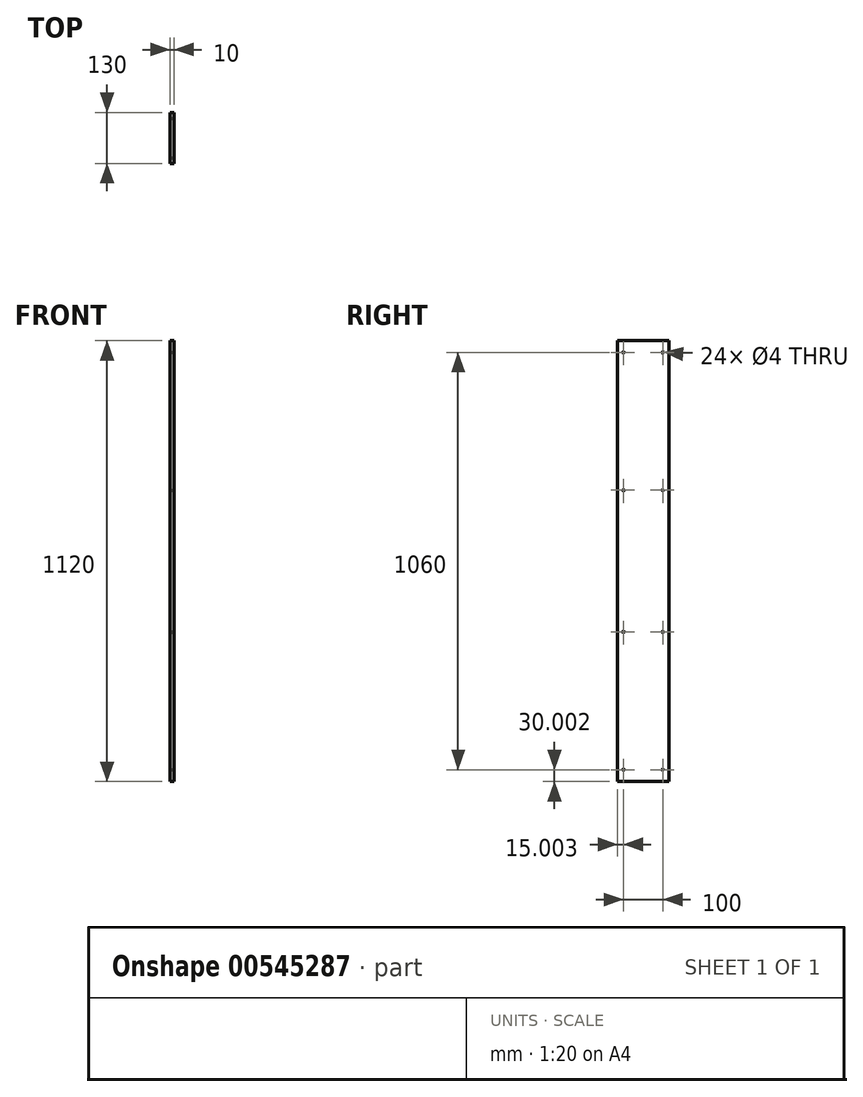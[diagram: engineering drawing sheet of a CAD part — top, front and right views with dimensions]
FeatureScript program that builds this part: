
annotation { "Feature Type Name" : "Feature", "Feature Type Description" : "" }
export const myFeature = defineFeature(function(context is Context, id is Id, definition is map)
    precondition{}
    {
        {
            var Q0;
            Q0=qCreatedBy(makeId("Right.planeOp"),FACE);
            var sketch = newSketch(context, id + "F0", { "sketchPlane" : qUnion([Q0])});
            skLineSegment(sketch, "E0.bottom", {"start": v(-510.9, -532.09) * mm, "end": v(-380.9, -532.09) * mm});
            skLineSegment(sketch, "E0.top", {"start": v(-510.9, 587.91) * mm, "end": v(-380.9, 587.91) * mm});
            skLineSegment(sketch, "E0.left", {"start": v(-510.9, -532.09) * mm, "end": v(-510.9, 587.91) * mm});
            skLineSegment(sketch, "E0.right", {"start": v(-380.9, -532.09) * mm, "end": v(-380.9, 587.91) * mm});
            skSolve(sketch);
        }
        {
            var Q0;
            Q0=makeQuery(id+"F0.imprint","IMPRINT",FACE,{"disambiguationData":[TD([[makeQuery(id+"F0.imprint","IMPRINT",EDGE,{"derivedFrom":sQuery(id+"F0.wireOp",EDGE,"E0.bottom")}),1.0]])]});
            extrude(context, id + "F1", {"entities" : qUnion([Q0]), "depth" : 10 * mm, "offsetDistance" : 25 * mm});
        }
        {
            var Q0;
            Q0=makeQuery(id+"F1.opExtrude","CAP_FACE",FACE,{"disambiguationData":[OSD([sQuery(id+"F0.wireOp",EDGE,"E0.bottom"),sQuery(id+"F0.wireOp",EDGE,"E0.top"),sQuery(id+"F0.wireOp",EDGE,"E0.left"),sQuery(id+"F0.wireOp",EDGE,"E0.right")])],"isStart":false});
            var sketch = newSketch(context, id + "F2", { "sketchPlane" : qUnion([Q0])});
            skLineSegment(sketch, "E1.bottom", {"start": v(-395.9, 557.91) * mm, "end": v(-495.9, 557.91) * mm, "construction": true});
            skLineSegment(sketch, "E1.top", {"start": v(-395.9, -502.09) * mm, "end": v(-495.9, -502.09) * mm, "construction": true});
            skLineSegment(sketch, "E1.left", {"start": v(-395.9, 557.91) * mm, "end": v(-395.9, -502.09) * mm, "construction": true});
            skLineSegment(sketch, "E1.right", {"start": v(-495.9, 557.91) * mm, "end": v(-495.9, -502.09) * mm, "construction": true});
            skPoint(sketch, "E2", {"position": v(-495.9, 557.91) * mm});
            skPoint(sketch, "E3", {"position": v(-395.9, 557.91) * mm});
            skPoint(sketch, "E4", {"position": v(-395.9, -502.09) * mm});
            skPoint(sketch, "E5", {"position": v(-495.9, -502.09) * mm});
            skLineSegment(sketch, "E6", {"start": v(-495.9, -152.09) * mm, "end": v(-395.9, -152.09) * mm, "construction": true});
            skLineSegment(sketch, "E7", {"start": v(-495.9, 207.91) * mm, "end": v(-395.9, 207.91) * mm, "construction": true});
            skPoint(sketch, "E8", {"position": v(-495.9, 207.91) * mm});
            skPoint(sketch, "E9", {"position": v(-395.9, 207.91) * mm});
            skPoint(sketch, "E10", {"position": v(-395.9, -152.09) * mm});
            skPoint(sketch, "E11", {"position": v(-495.9, -152.09) * mm});
            skSolve(sketch);
        }
        {
            var Q0;
            Q0=sQuery(id+"F2.wireOp",VERTEX,"E2");
            var Q1;
            Q1=sQuery(id+"F2.wireOp",VERTEX,"E3");
            var Q2;
            Q2=sQuery(id+"F2.wireOp",VERTEX,"E9");
            var Q3;
            Q3=sQuery(id+"F2.wireOp",VERTEX,"E8");
            var Q4;
            Q4=sQuery(id+"F2.wireOp",VERTEX,"E10");
            var Q5;
            Q5=sQuery(id+"F2.wireOp",VERTEX,"E11");
            var Q6;
            Q6=sQuery(id+"F2.wireOp",VERTEX,"E5");
            var Q7;
            Q7=sQuery(id+"F2.wireOp",VERTEX,"E4");
            var Q8;
            Q8=makeQuery(id+"F1.opExtrude","SWEPT_BODY",BODY,{"disambiguationData":[OSD([sQuery(id+"F0.wireOp",EDGE,"E0.bottom"),sQuery(id+"F0.wireOp",EDGE,"E0.top"),sQuery(id+"F0.wireOp",EDGE,"E0.left"),sQuery(id+"F0.wireOp",EDGE,"E0.right")])]});
            hole(context, id + "F3", {"style" : HoleStyle.SIMPLE, "endStyle" : HoleEndStyle.THROUGH, "holeDiameter" : 4 * mm, "isTappedThrough" : true, "tappedDepth" : 12 * mm, "tapClearance" : 3, "startFromSketch" : true, "locations" : qUnion([Q0, Q1, Q2, Q3, Q4, Q5, Q6, Q7]), "scope" : qUnion([Q8])});
        }
    });
